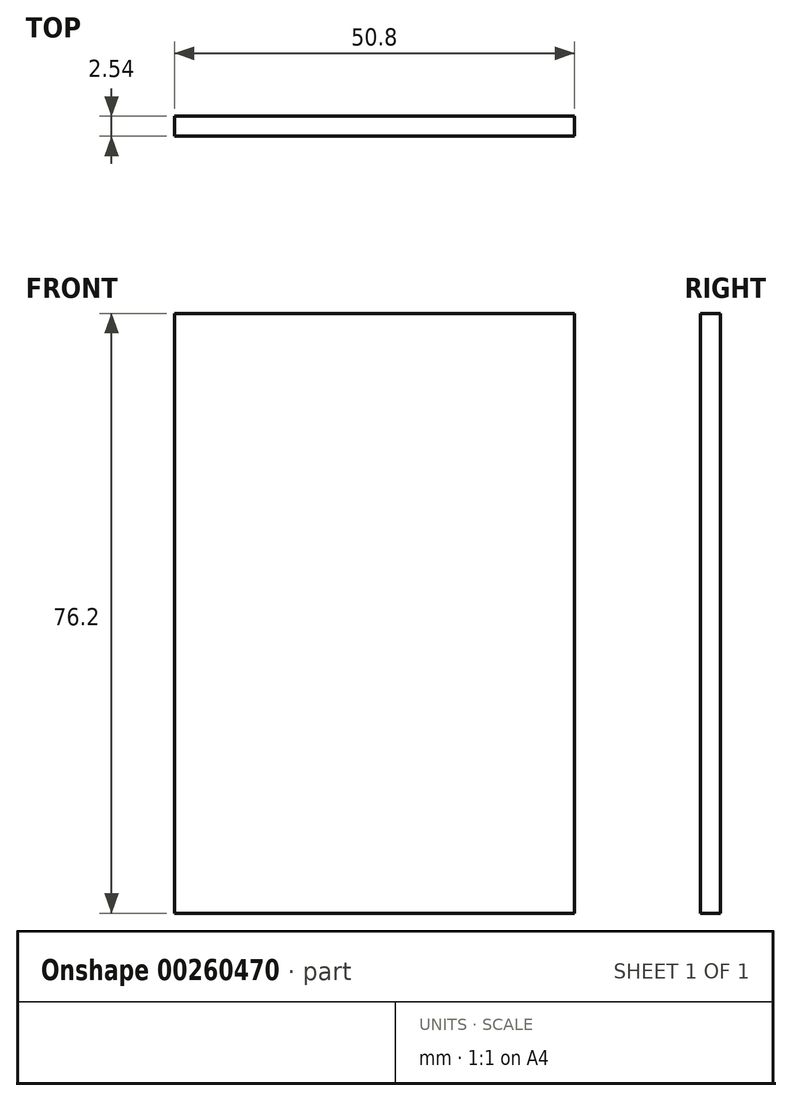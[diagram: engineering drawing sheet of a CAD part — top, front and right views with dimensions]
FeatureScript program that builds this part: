
annotation { "Feature Type Name" : "Feature", "Feature Type Description" : "" }
export const myFeature = defineFeature(function(context is Context, id is Id, definition is map)
    precondition{}
    {
        {
            var Q0;
            Q0=qCreatedBy(makeId("Front.planeOp"),FACE);
            var sketch = newSketch(context, id + "F0", { "sketchPlane" : qUnion([Q0])});
            skLineSegment(sketch, "E0.bottom", {"start": v(25.4, 34.2) * mm, "end": v(-25.4, 34.2) * mm});
            skLineSegment(sketch, "E0.top", {"start": v(25.4, -42) * mm, "end": v(-25.4, -42) * mm});
            skLineSegment(sketch, "E0.left", {"start": v(25.4, 34.2) * mm, "end": v(25.4, -42) * mm});
            skLineSegment(sketch, "E0.right", {"start": v(-25.4, 34.2) * mm, "end": v(-25.4, -42) * mm});
            skPoint(sketch, "E0.middle", {"position": v(0, -3.9) * mm});
            skSolve(sketch);
        }
        {
            var Q0;
            Q0=makeQuery(id+"F0.imprint","IMPRINT",FACE,{"disambiguationData":[TD([[makeQuery(id+"F0.imprint","IMPRINT",EDGE,{"derivedFrom":sQuery(id+"F0.wireOp",EDGE,"E0.bottom")}),1.0]])]});
            extrude(context, id + "F1", {"entities" : qUnion([Q0]), "depth" : 2.54 * mm});
        }
    });
